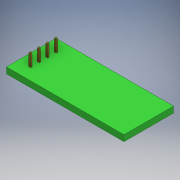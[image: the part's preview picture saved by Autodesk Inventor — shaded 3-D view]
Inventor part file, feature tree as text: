
AUTODESK INVENTOR PART (.ipt)
format: ipt  version: 2018.3 (Build 223284000, 284)  size: 252,928 bytes
history: native  units: mm
features: chamfer x16, extrude x8, sketch x8
ambient origin geometry x8: Origin, YZ Plane, XZ Plane, XY Plane, X Axis, Y Axis, Z Axis, Center Point
bodies: Solid1 (feature_tree)
feature tree (32):
  extrude  "Extrusion1"  Depth=13.7mm
  extrude  "Extrusion2"  Depth=6.0mm
  extrude  "Extrusion3"  Depth=0.5mm TaperAngle=0.0deg
  chamfer  "Chamfer1"  Distance=3.5mm
  chamfer  "Chamfer2"  Distance=0.5mm Angle=45.0deg
  extrude  "Extrusion4"  Depth=1.94mm
  chamfer  "Chamfer3"  Distance=3.5mm
  chamfer  "Chamfer4"  Distance=0.5mm Angle=45.0deg
  extrude  "Extrusion5"  Depth=1.94mm
  chamfer  "Chamfer5"  Distance=3.5mm
  chamfer  "Chamfer6"  Distance=0.5mm Angle=45.0deg
  chamfer  "Chamfer7"  Distance=0.5mm Angle=45.0deg
  chamfer  "Chamfer8"  Distance=0.5mm Angle=45.0deg
  chamfer  "Chamfer17"  Distance=0.5mm Angle=45.0deg
  sketch  "Sketch1"  dims[d0=32.5mm d1=13.7mm]
  sketch  "Sketch2"  dims[d2=1.7mm d3=0.0mm d4=6.0mm]
  sketch  "Sketch3"  dims[d5=6.0mm d6=0.5mm d7=0.0mm]
  sketch  "Sketch4"  dims[d8=0.6mm]
  sketch  "Sketch5"  dims[d9=0.4mm d10=3.5mm d11=0.0mm d12=0.15mm d13=0.5mm d14=45.0deg]
  sketch  "Sketch6"  dims[d15=0.15mm d16=0.5mm d17=45.0deg d19=1.94mm d20=3.5mm d21=0.0mm d22=0.15mm d23=0.5mm d24=45.0deg]
  sketch  "Sketch7"  dims[d25=0.15mm d26=0.5mm d27=45.0deg d28=1.94mm]
  sketch  "Sketch8"  dims[d29=1.94mm d30=3.5mm d31=0.0mm d32=0.15mm d33=0.5mm d34=45.0deg d35=0.15mm d36=0.5mm d37=45.0deg d38=0.15mm d39=0.5mm d40=45.0deg d41=0.15mm d42=0.5mm d43=45.0deg d44=3.0mm d45=3.14mm d49=5.0mm d50=3.14mm d51=0.6mm d52=0.4mm d54=0.0mm d55=3.5mm d56=45.0deg d57=0.5mm d58=0.15mm d59=45.0deg d60=0.5mm d61=0.15mm d64=0.0mm d65=3.5mm d66=45.0deg d67=0.5mm d68=0.15mm d69=45.0deg d70=0.5mm d71=0.15mm d75=0.0mm d76=3.5mm d80=45.0deg d81=0.5mm d82=0.15mm d83=45.0deg d84=0.5mm d85=0.15mm d86=45.0deg d87=0.5mm d88=0.15mm d89=1.94mm d90=0.4mm d91=0.6mm d92=1.94mm d96=0.6mm d97=0.6mm d98=0.4mm d99=0.4mm d100=0.6mm d101=0.4mm d102=0.15mm d103=0.5mm d104=45.0deg]
  extrude  "Extrusion6"  Depth=3.0mm
  extrude  "Extrusion7"  Depth=3.14mm
  extrude  "Extrusion8"  Depth=0.5mm TaperAngle=45.0deg
  chamfer  "Chamfer9"  Distance=0.5mm Angle=45.0deg
  chamfer  "Chamfer10"  Distance=3.5mm
  chamfer  "Chamfer11"  Distance=0.5mm Angle=45.0deg
  chamfer  "Chamfer12"  Distance=0.5mm Angle=45.0deg
  chamfer  "Chamfer14"  Distance=3.5mm
  chamfer  "Chamfer15"  Distance=0.5mm Angle=45.0deg
  chamfer  "Chamfer16"  Distance=0.5mm Angle=45.0deg
